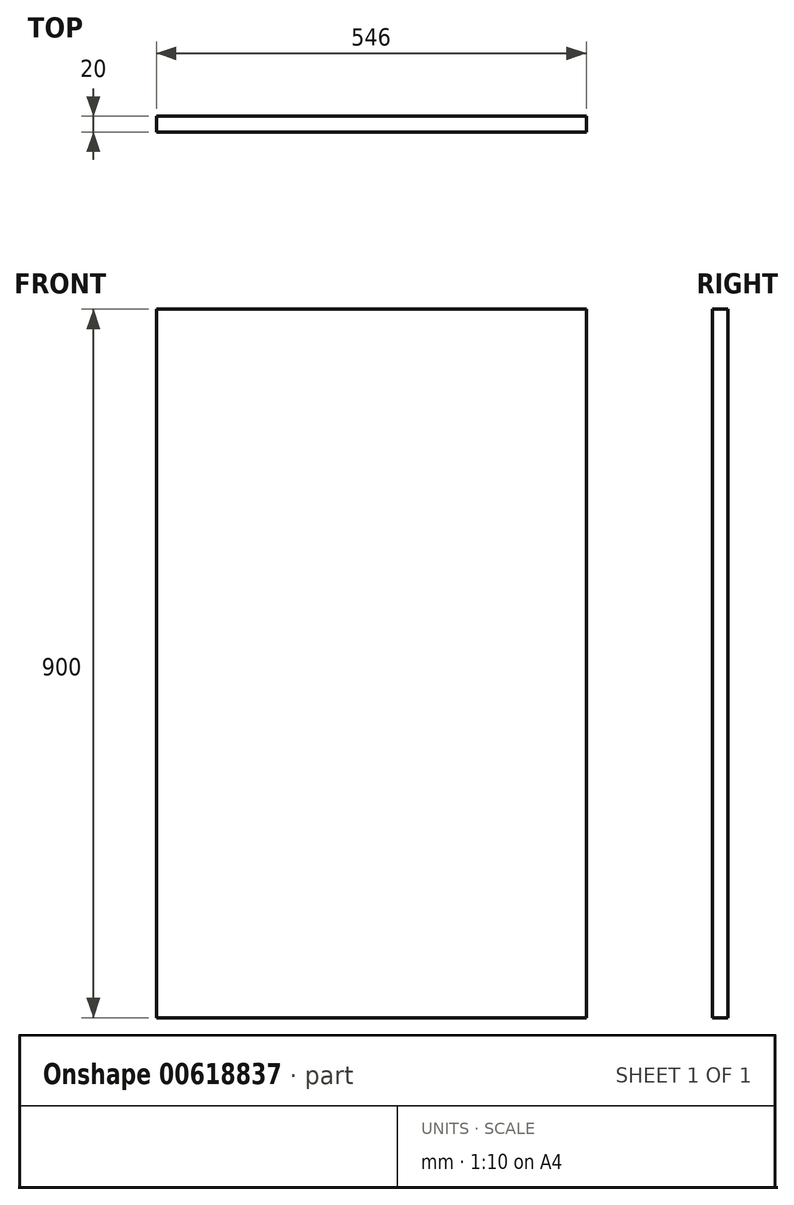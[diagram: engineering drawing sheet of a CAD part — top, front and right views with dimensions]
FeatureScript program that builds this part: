
annotation { "Feature Type Name" : "Feature", "Feature Type Description" : "" }
export const myFeature = defineFeature(function(context is Context, id is Id, definition is map)
    precondition{}
    {
        {
            var Q0;
            Q0=qCreatedBy(makeId("Front.planeOp"),FACE);
            var sketch = newSketch(context, id + "F0", { "sketchPlane" : qUnion([Q0])});
            skLineSegment(sketch, "E0.bottom", {"start": v(-273, 450) * mm, "end": v(273, 450) * mm});
            skLineSegment(sketch, "E0.top", {"start": v(-273, -450) * mm, "end": v(273, -450) * mm});
            skLineSegment(sketch, "E0.left", {"start": v(-273, 450) * mm, "end": v(-273, -450) * mm});
            skLineSegment(sketch, "E0.right", {"start": v(273, 450) * mm, "end": v(273, -450) * mm});
            skPoint(sketch, "E0.middle", {"position": v(0, 0) * mm});
            skSolve(sketch);
        }
        {
            var Q0;
            Q0 = qSketchRegion(id + "F0", true);
            extrude(context, id + "F1", {"entities" : qUnion([Q0]), "depth" : 20 * mm, "offsetDistance" : 25 * mm});
        }
    });
